# Revit family: 306_e29e9fc0855a42fe8b6e8100d524ff
name_source: partatom
category: Pipe Accessories
units: mm (PartAtom-declared; Revit-internal decimal feet)

## family parameters
Always vertical = Yes
Cut with Voids When Loaded = No
Part Type = Valve - Breaks Into
Round Connector Dimension = Use Diameter
Shared = No
Work Plane-Based = No

## types (8) — shared parameters
CAT0 = Yes
Description = 2-way Control valve VLA121, PN16 internal thread
L2D_Min = 3048 mm
Manufacturer = ESBE
QmdConnectorList = 301;D;302;D
URL = http://www.esbe.eu
Z4 = 13 mm
Z5 = 4 mm  [stored 0.0131234 ft]
Z6 = 2 mm  [stored 0.00656168 ft]
Z7 = 15 mm  [stored 0.0492126 ft]
magiPartTypeId = 306
magiProductFamilyId = e29e9fc0855a42fe8b6e8100d524ff

## per-type parameters (varying)
- VLA121 PN16 RP1 1/2 DN40-25: CenSd_D6_6=19 mm; CenSd_DN_6=33 mm; D=40 mm; D1=42 mm; D10=30 mm  [stored 0.0984252 ft]; D2=34 mm; D3=30 mm  [stored 0.0984252 ft]; D4=27 mm; D5=29 mm; D6=22 mm; D7=15 mm  [stored 0.0492126 ft]; D8=8 mm  [stored 0.0262467 ft]; D9=7 mm  [stored 0.0229659 ft]; DN=38 mm; DN1=32 mm  [stored 0.104987 ft]; DN2=30 mm  [stored 0.0984252 ft]; H3=50 mm; H4=42 mm; L2=111 mm; L2D=150 mm; LT2=75 mm; W2D=40 mm; X1=5 mm  [stored 0.0164042 ft]; XN=15 mm  [stored 0.0492126 ft]; XN__ve=-15 mm  [stored -0.0492126 ft]; Z1=14 mm  [stored 0.0459318 ft]; Z11=11 mm; Z2=63 mm; magiProductId=107dd482e02242b6b0fa765d5bd74c
- VLA121 PN16 RP3/4 DN20-6,3: CenSd_D6_6=12 mm  [stored 0.0393701 ft]; CenSd_DN_6=16 mm; D=20 mm; D1=28 mm; D10=15 mm  [stored 0.0492126 ft]; D2=22 mm; D3=20 mm  [stored 0.0656168 ft]; D4=18 mm; D5=19 mm; D6=14 mm  [stored 0.0459318 ft]; D7=10 mm  [stored 0.0328084 ft]; D8=5 mm  [stored 0.0164042 ft]; D9=5 mm  [stored 0.0164042 ft]; DN=19 mm; DN1=16 mm; DN2=15 mm  [stored 0.0492126 ft]; H3=40 mm; H4=30 mm  [stored 0.0984252 ft]; L2=74 mm; L2D=100 mm; LT2=50 mm; W2D=20 mm  [stored 0.0656168 ft]; X1=3 mm  [stored 0.00984252 ft]; XN=10 mm  [stored 0.0328084 ft]; XN__ve=-10 mm  [stored -0.0328084 ft]; Z1=13 mm; Z11=8 mm  [stored 0.0262467 ft]; Z2=45 mm; magiProductId=b8fe9e7c7a8c428f8bebaeed6f4070
- VLA121 PN16 RP2 DN50-38: CenSd_D6_6=22 mm; CenSd_DN_6=41 mm; D=50 mm; D1=50 mm; D10=38 mm; D2=40 mm; D3=36 mm; D4=33 mm; D5=34 mm; D6=26 mm; D7=18 mm; D8=9 mm  [stored 0.0295276 ft]; D9=8 mm  [stored 0.0262467 ft]; DN=48 mm; DN1=40 mm; DN2=38 mm; H3=59 mm; H4=53 mm; L2=133 mm; L2D=180 mm; LT2=90 mm; W2D=50 mm; X1=5 mm  [stored 0.0164042 ft]; XN=18 mm; XN__ve=-18 mm; Z1=14 mm  [stored 0.0459318 ft]; Z11=13 mm; Z2=80 mm; magiProductId=9bf992274bf4403b8f22a96a12b8a1
- VLA121 PN16 RP1/2 DN15-4,0: CenSd_D6_6=11 mm; CenSd_DN_6=12 mm  [stored 0.0393701 ft]; D=15 mm; D1=24 mm; D10=11 mm; D2=19 mm; D3=17 mm; D4=15 mm  [stored 0.0492126 ft]; D5=16 mm; D6=12 mm  [stored 0.0393701 ft]; D7=9 mm  [stored 0.0295276 ft]; D8=4 mm  [stored 0.0131234 ft]; D9=4 mm  [stored 0.0131234 ft]; DN=14 mm  [stored 0.0459318 ft]; DN1=12 mm  [stored 0.0393701 ft]; DN2=11 mm; H3=38 mm; H4=24 mm; L2=63 mm; L2D=85 mm; LT2=43 mm; W2D=15 mm  [stored 0.0492126 ft]; X1=3 mm  [stored 0.00984252 ft]; XN=9 mm  [stored 0.0295276 ft]; XN__ve=-9 mm; Z1=15 mm  [stored 0.0492126 ft]; Z11=6 mm  [stored 0.019685 ft]; Z2=36 mm; magiProductId=37b39d390a404fa3b851c25d218b4f
- VLA121 PN16 RP1/2 DN15-2,5: CenSd_D6_6=11 mm; CenSd_DN_6=12 mm  [stored 0.0393701 ft]; D=15 mm; D1=24 mm; D10=11 mm; D2=19 mm; D3=17 mm; D4=15 mm  [stored 0.0492126 ft]; D5=16 mm; D6=12 mm  [stored 0.0393701 ft]; D7=9 mm  [stored 0.0295276 ft]; D8=4 mm  [stored 0.0131234 ft]; D9=4 mm  [stored 0.0131234 ft]; DN=14 mm  [stored 0.0459318 ft]; DN1=12 mm  [stored 0.0393701 ft]; DN2=11 mm; H3=38 mm; H4=24 mm; L2=63 mm; L2D=85 mm; LT2=43 mm; W2D=15 mm  [stored 0.0492126 ft]; X1=3 mm  [stored 0.00984252 ft]; XN=9 mm  [stored 0.0295276 ft]; XN__ve=-9 mm; Z1=15 mm  [stored 0.0492126 ft]; Z11=6 mm  [stored 0.019685 ft]; Z2=36 mm; magiProductId=7a579ad872dd4f59b36caf6c77db66
- VLA121 PN16 RP1/2 DN15-1,6: CenSd_D6_6=11 mm; CenSd_DN_6=12 mm  [stored 0.0393701 ft]; D=15 mm; D1=24 mm; D10=11 mm; D2=19 mm; D3=17 mm; D4=15 mm  [stored 0.0492126 ft]; D5=16 mm; D6=12 mm  [stored 0.0393701 ft]; D7=9 mm  [stored 0.0295276 ft]; D8=4 mm  [stored 0.0131234 ft]; D9=4 mm  [stored 0.0131234 ft]; DN=14 mm  [stored 0.0459318 ft]; DN1=12 mm  [stored 0.0393701 ft]; DN2=11 mm; H3=38 mm; H4=24 mm; L2=63 mm; L2D=85 mm; LT2=43 mm; W2D=15 mm  [stored 0.0492126 ft]; X1=3 mm  [stored 0.00984252 ft]; XN=9 mm  [stored 0.0295276 ft]; XN__ve=-9 mm; Z1=15 mm  [stored 0.0492126 ft]; Z11=6 mm  [stored 0.019685 ft]; Z2=36 mm; magiProductId=065c5ecd664643f5bbceab49664c60
- VLA121 PN16 RP1 DN25-10: CenSd_D6_6=14 mm  [stored 0.0459318 ft]; CenSd_DN_6=21 mm  [stored 0.0688976 ft]; D=25 mm; D1=32 mm  [stored 0.104987 ft]; D10=19 mm; D2=26 mm; D3=23 mm; D4=21 mm  [stored 0.0688976 ft]; D5=22 mm; D6=17 mm; D7=12 mm  [stored 0.0393701 ft]; D8=6 mm  [stored 0.019685 ft]; D9=5 mm  [stored 0.0164042 ft]; DN=24 mm; DN1=20 mm  [stored 0.0656168 ft]; DN2=19 mm; H3=40 mm; H4=34 mm; L2=85 mm; L2D=115 mm; LT2=58 mm; W2D=25 mm  [stored 0.082021 ft]; X1=3 mm  [stored 0.00984252 ft]; XN=12 mm  [stored 0.0393701 ft]; XN__ve=-12 mm; Z1=11 mm; Z11=9 mm  [stored 0.0295276 ft]; Z2=51 mm; magiProductId=29f2c5e65b7345aaa94f98dade89fb
- VLA121 PN16 RP1 1/4 DN32-16: CenSd_D6_6=16 mm; CenSd_DN_6=26 mm; D=32 mm; D1=36 mm; D10=24 mm; D2=29 mm; D3=26 mm; D4=24 mm; D5=25 mm  [stored 0.082021 ft]; D6=19 mm; D7=13 mm; D8=7 mm  [stored 0.0229659 ft]; D9=6 mm  [stored 0.019685 ft]; DN=30 mm  [stored 0.0984252 ft]; DN1=26 mm; DN2=24 mm; H3=41 mm; H4=35 mm; L2=96 mm; L2D=130 mm; LT2=65 mm; W2D=32 mm  [stored 0.104987 ft]; X1=4 mm  [stored 0.0131234 ft]; XN=13 mm; XN__ve=-13 mm; Z1=11 mm; Z11=9 mm  [stored 0.0295276 ft]; Z2=53 mm; magiProductId=48f097ad14134ad0b7541736e62e2e

note: column(s) folded — value = type name in every type: magiProductCode

note: [stored X ft] marks values corroborated as IEEE doubles in the binary element streams (Revit-internal decimal feet)

## geometry (parser evidence)
native form markers: Sweep x3
no freeform markers — native parametric forms only
